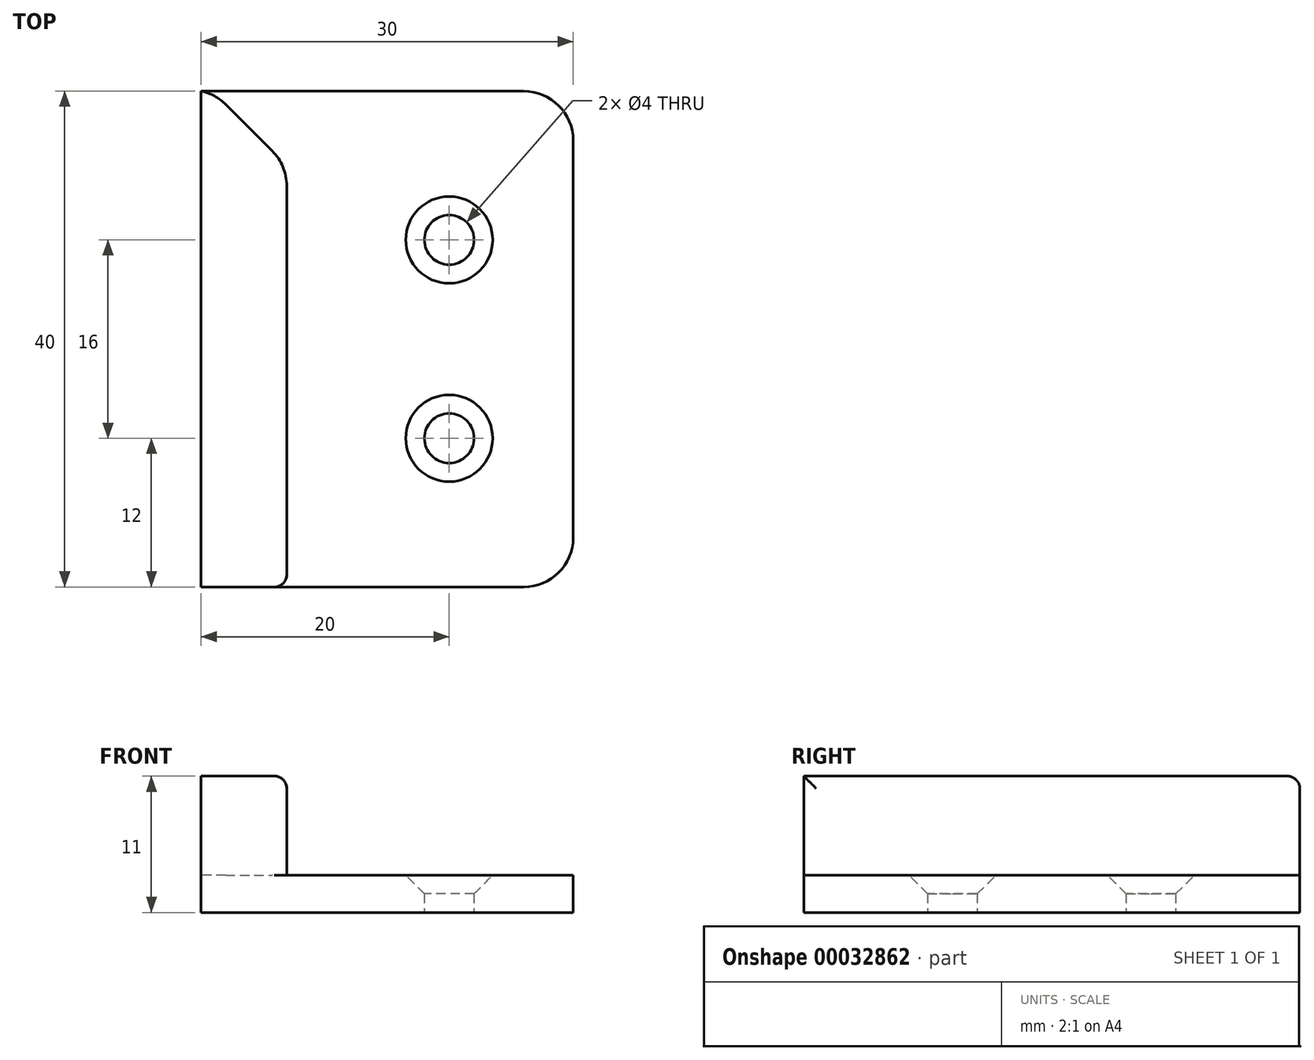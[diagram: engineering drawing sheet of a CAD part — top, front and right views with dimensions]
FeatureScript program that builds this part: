
annotation { "Feature Type Name" : "Feature", "Feature Type Description" : "" }
export const myFeature = defineFeature(function(context is Context, id is Id, definition is map)
    precondition{}
    {
        {
            var Q0;
            Q0=qCreatedBy(makeId("Top.planeOp"),FACE);
            var sketch = newSketch(context, id + "F0", { "sketchPlane" : qUnion([Q0])});
            skLineSegment(sketch, "E0", {"start": v(0, 0) * mm, "end": v(30, 0) * mm});
            skLineSegment(sketch, "E1", {"start": v(30, 0) * mm, "end": v(30, 40) * mm});
            skLineSegment(sketch, "E2", {"start": v(30, 40) * mm, "end": v(0, 40) * mm});
            skLineSegment(sketch, "E3", {"start": v(0, 40) * mm, "end": v(0, 0) * mm});
            skLineSegment(sketch, "E4", {"start": v(6.9, 40) * mm, "end": v(6.9, 0) * mm});
            skLineSegment(sketch, "E5", {"start": v(0, 33.02) * mm, "end": v(6.9, 33.02) * mm, "construction": true});
            skCircle(sketch, "E6", {"center": v(20, 28) * mm, "radius": 2 * mm});
            skCircle(sketch, "E7", {"center": v(20, 12) * mm, "radius": 2 * mm});
            skLineSegment(sketch, "E8", {"start": v(20, 12) * mm, "end": v(0, 12) * mm, "construction": true});
            skLineSegment(sketch, "E9", {"start": v(20, 40) * mm, "end": v(20, 28) * mm, "construction": true});
            skLineSegment(sketch, "E10", {"start": v(20, 28) * mm, "end": v(20, 12) * mm, "construction": true});
            skSolve(sketch);
        }
        {
            var Q0;
            {var subQ1=sQuery(id+"F0.wireOp",EDGE,"E3");Q0=makeQuery(id+"F0.imprint","IMPRINT",FACE,{"disambiguationData":[TD([[makeQuery(id+"F0.imprint","IMPRINT",EDGE,{"derivedFrom":subQ1}),1.0]])]});}
            extrude(context, id + "F1", {"entities" : qUnion([Q0]), "depth" : 11 * mm});
        }
        {
            var Q0;
            {var subQ2=sQuery(id+"F0.wireOp",EDGE,"E1");Q0=makeQuery(id+"F0.imprint","IMPRINT",FACE,{"disambiguationData":[TD([[makeQuery(id+"F0.imprint","IMPRINT",EDGE,{"derivedFrom":subQ2}),1.0]])]});}
            extrude(context, id + "F2", {"entities" : qUnion([Q0]), "operationType" : NewBodyOperationType.ADD, "depth" : 3 * mm});
        }
        {
            var Q0;
            Q0=makeQuery(id+"F1.opExtrude","SWEPT_EDGE",EDGE,{"disambiguationData":[OSD([sQuery(id+"F0.wireOp",EDGE,"E2"),sQuery(id+"F0.wireOp",EDGE,"E4")])]});
            chamfer(context, id + "F3", {"entities" : qUnion([Q0]), "width" : 6 * mm, "tangentPropagation" : true});
        }
        {
            var Q0;
            {var subQ0=sQuery(id+"F0.wireOp",EDGE,"E2");Q0=makeQuery(id+"F3.opChamfer","BLEND_EDGE",EDGE,{"blendedFrom":[makeQuery(id+"F1.opExtrude","SWEPT_EDGE",EDGE,{"disambiguationData":[OSD([subQ0,sQuery(id+"F0.wireOp",EDGE,"E4")])]}),makeQuery(id+"F2.boolean.opBoolean","MERGE",FACE,{"derivedFrom":[makeQuery(id+"F1.opExtrude","SWEPT_FACE",FACE,{"disambiguationData":[OSD([subQ0])]}),makeQuery(id+"F2.opExtrude","SWEPT_FACE",FACE,{"disambiguationData":[OSD([subQ0])]})]})],"blendedInto":[makeQuery(id+"F2.boolean.opBoolean","MERGE",FACE,{"derivedFrom":[makeQuery(id+"F1.opExtrude","SWEPT_FACE",FACE,{"disambiguationData":[OSD([subQ0])]}),makeQuery(id+"F2.opExtrude","SWEPT_FACE",FACE,{"disambiguationData":[OSD([subQ0])]})]})]});}
            var Q1;
            {var subQ0=sQuery(id+"F0.wireOp",EDGE,"E4");Q1=makeQuery(id+"F3.opChamfer","BLEND_EDGE",EDGE,{"blendedFrom":[makeQuery(id+"F1.opExtrude","SWEPT_EDGE",EDGE,{"disambiguationData":[OSD([sQuery(id+"F0.wireOp",EDGE,"E2"),subQ0])]}),makeQuery(id+"F1.opExtrude","SWEPT_FACE",FACE,{"disambiguationData":[OSD([subQ0])]})],"blendedInto":[makeQuery(id+"F1.opExtrude","SWEPT_FACE",FACE,{"disambiguationData":[OSD([subQ0])]})]});}
            var Q2;
            Q2=makeQuery(id+"F2.opExtrude","SWEPT_EDGE",EDGE,{"disambiguationData":[OSD([sQuery(id+"F0.wireOp",EDGE,"E1"),sQuery(id+"F0.wireOp",EDGE,"E2")])]});
            var Q3;
            Q3=makeQuery(id+"F2.opExtrude","SWEPT_EDGE",EDGE,{"disambiguationData":[OSD([sQuery(id+"F0.wireOp",EDGE,"E0"),sQuery(id+"F0.wireOp",EDGE,"E1")])]});
            fillet(context, id + "F4", {"entities" : qUnion([Q0, Q1, Q2, Q3]), "radius" : 4 * mm, "tangentPropagation" : true, "allowEdgeOverflow" : false});
        }
        {
            var Q0;
            Q0=makeQuery(id+"F2.opExtrude","CAP_EDGE",EDGE,{"disambiguationData":[OSD([sQuery(id+"F0.wireOp",EDGE,"E6")])],"isStart":false});
            var Q1;
            Q1=makeQuery(id+"F2.opExtrude","CAP_EDGE",EDGE,{"disambiguationData":[OSD([sQuery(id+"F0.wireOp",EDGE,"E7")])],"isStart":false});
            chamfer(context, id + "F5", {"entities" : qUnion([Q0, Q1]), "width" : 1.5 * mm, "tangentPropagation" : true});
        }
        {
            var Q0;
            Q0=makeQuery(id+"F1.opExtrude","SWEPT_EDGE",EDGE,{"disambiguationData":[OSD([sQuery(id+"F0.wireOp",EDGE,"E0"),sQuery(id+"F0.wireOp",EDGE,"E4")])]});
            var Q1;
            Q1=makeQuery(id+"F1.opExtrude","CAP_EDGE",EDGE,{"disambiguationData":[OSD([sQuery(id+"F0.wireOp",EDGE,"E4")])],"isStart":false});
            fillet(context, id + "F6", {"entities" : qUnion([Q0, Q1]), "radius" : 1 * mm, "tangentPropagation" : true, "allowEdgeOverflow" : false});
        }
    });
